# Revit family: Urinal_Washdown-Top_Spud-American_Standard-Decorum-6042.005
name_source: partatom
category: Plumbing Fixtures
units: mm (PartAtom-declared; Revit-internal decimal feet)

## family parameters
Cut with Voids When Loaded = No
Host = Face
OmniClass Number = 23.45.05.21.11.21
OmniClass Title = Urinals
Part Type = Normal
Room Calculation Point = No
Round Connector Dimension = Use Radius
Shared = Yes

## types (2) — shared parameters
ADA Compliant = Yes
Assembly Code = D2010210
CW Connection = Yes
CWFU = 5
Cold Water Connection Diameter = 3/4"
Cold Water Connection Height = 11 1/2"
Cold Water Connection Radius = 3/8"
Cold Water Connection Width = 4 3/4"
Default Elevation = 24"
Flush Rate = 0.125 GPF (0.47 Lpf)
HW Connection = No
Height = 21 1/2"
Installation Type = Wall Hung
Length = 14"
Manufacturer = American Standard
Material = Vitreous China-American Standard-020-White
Price = Prices may vary. Please consult Manufacturer Representative for most up-to-date price list.
Product Documentation Link = https://www.americanstandard-us.com
Product Page URL = https://www.americanstandard-us.com
Revised Date = 12/04/2020
URL = http://www.americanstandard-us.com
Vent Connection = No
WFU = 5
Warranty Information = 1 Year Limated Warranty
Waste Connection = Yes
Waste Connection Diameter = 2"
Waste Connection Height = 2 1/2"
Waste Connection Radius = 1"
Width = 13 5/16"
zero-valued in all types: HWFU

## per-type parameters (varying)
| type | Back Spud | Description | Flushvalve | Top Spud |
| 6042.005.020 | No | Decorum 0.125 gpf Urinal System with Manual Flush Valve | Flush_Valve-Urinal-American_Standard-Exposed-Top_Spud-Manual_Series : 6045.013 | Yes |
| 6043.005.020 | Yes | Decorum 0.125 gpf Urinal System with Selectronic Battery-Powered Flush Valve | Flush_Valve-Urinal_Exposed-American_Standard-Selectronic_Series : 6063.013.002 | No |

note: column(s) folded — value = type name in every type: Model

## geometry (parser evidence)
native form markers: Sweep x6
no freeform markers — native parametric forms only
